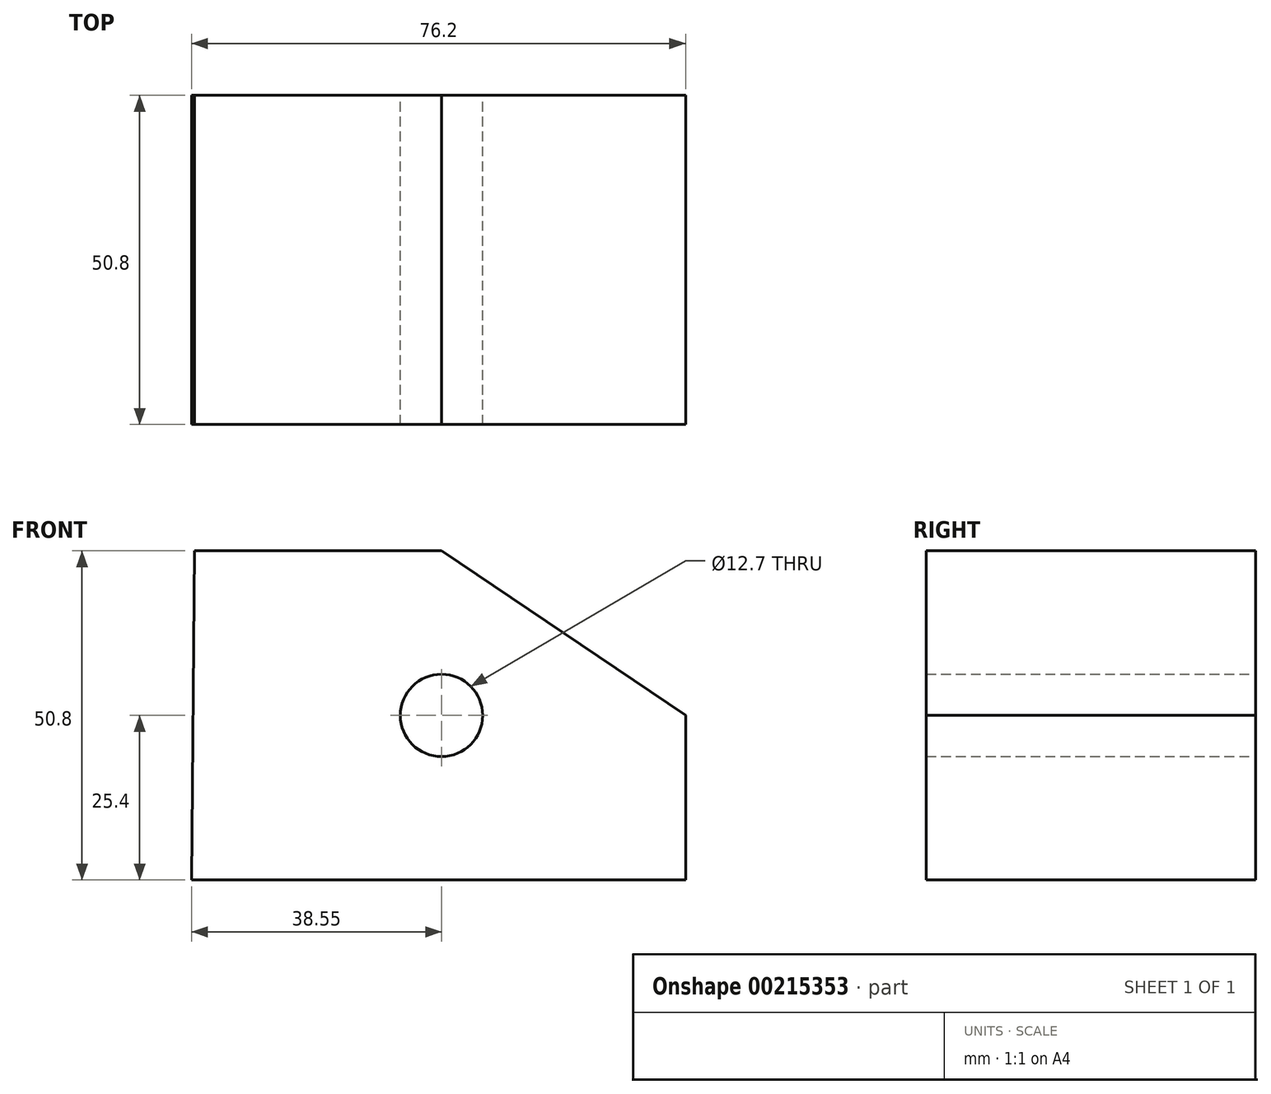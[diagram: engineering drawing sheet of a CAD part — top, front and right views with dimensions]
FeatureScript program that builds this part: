
annotation { "Feature Type Name" : "Feature", "Feature Type Description" : "" }
export const myFeature = defineFeature(function(context is Context, id is Id, definition is map)
    precondition{}
    {
        {
            var Q0;
            Q0=qCreatedBy(makeId("Front.planeOp"),FACE);
            var sketch = newSketch(context, id + "F0", { "sketchPlane" : qUnion([Q0])});
            skCircle(sketch, "E0", {"center": v(0, 0) * mm, "radius": 6.35 * mm});
            skLineSegment(sketch, "E1", {"start": v(-38.55, -25.4) * mm, "end": v(37.65, -25.4) * mm});
            skLineSegment(sketch, "E2", {"start": v(37.65, -25.4) * mm, "end": v(37.65, 0) * mm});
            skLineSegment(sketch, "E3", {"start": v(37.65, 0) * mm, "end": v(0, 25.4) * mm});
            skLineSegment(sketch, "E4", {"start": v(0, 25.4) * mm, "end": v(-38.1, 25.4) * mm});
            skLineSegment(sketch, "E5", {"start": v(-38.1, 25.4) * mm, "end": v(-38.55, -25.4) * mm});
            skSolve(sketch);
        }
        {
            var Q0;
            Q0=makeQuery(id+"F0.imprint","IMPRINT",FACE,{"disambiguationData":[TD([[makeQuery(id+"F0.imprint","IMPRINT",EDGE,{"derivedFrom":sQuery(id+"F0.wireOp",EDGE,"E0")}),-1.0]])]});
            extrude(context, id + "F1", {"entities" : qUnion([Q0]), "endBound" : BoundingType.SYMMETRIC, "depth" : 50.8 * mm});
        }
    });
